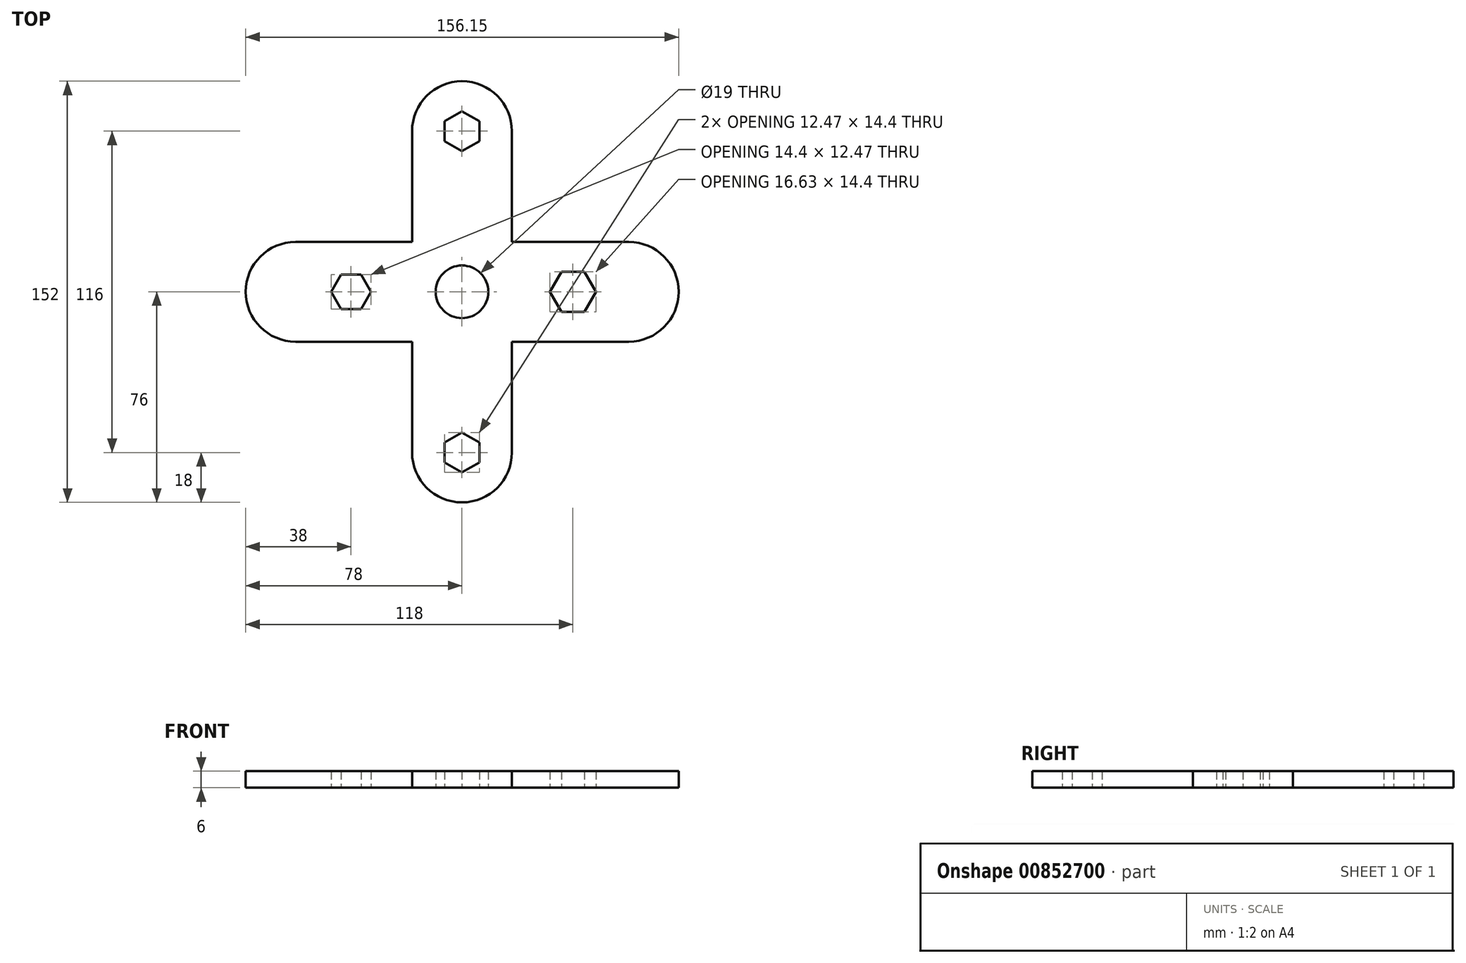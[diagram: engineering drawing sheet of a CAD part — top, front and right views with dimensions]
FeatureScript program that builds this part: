
annotation { "Feature Type Name" : "Feature", "Feature Type Description" : "" }
export const myFeature = defineFeature(function(context is Context, id is Id, definition is map)
    precondition{}
    {
        {
            var Q0;
            Q0=qCreatedBy(makeId("Top.planeOp"),FACE);
            var sketch = newSketch(context, id + "F0", { "sketchPlane" : qUnion([Q0])});
            skCircle(sketch, "E0", {"center": v(0, 0) * mm, "radius": 9.5 * mm});
            skLineSegment(sketch, "E1.bottom", {"start": v(0, 0) * mm, "end": v(-40, 0) * mm});
            skLineSegment(sketch, "E1.top", {"start": v(0, 18) * mm, "end": v(-40, 18) * mm});
            skLineSegment(sketch, "E1.left", {"start": v(0, 0) * mm, "end": v(0, 18) * mm});
            skLineSegment(sketch, "E2.bottom", {"start": v(0, 0) * mm, "end": v(40, 0) * mm});
            skLineSegment(sketch, "E2.top", {"start": v(0, 18) * mm, "end": v(40, 18) * mm});
            skLineSegment(sketch, "E3.top", {"start": v(0, -18) * mm, "end": v(-40, -18) * mm});
            skLineSegment(sketch, "E3.left", {"start": v(0, 0) * mm, "end": v(0, -18) * mm});
            skLineSegment(sketch, "E4.top", {"start": v(0, -18) * mm, "end": v(40, -18) * mm});
            skLineSegment(sketch, "E5.left", {"start": v(0, 0) * mm, "end": v(0, 40) * mm});
            skLineSegment(sketch, "E5.right", {"start": v(-18, 0) * mm, "end": v(-18, 40) * mm});
            skPoint(sketch, "E6.oppositeSnap0", {"position": v(20, 0) * mm});
            skLineSegment(sketch, "E6.bottom", {"start": v(0, 0) * mm, "end": v(20, 0) * mm});
            skLineSegment(sketch, "E6.left", {"start": v(0, 0) * mm, "end": v(0, 58) * mm});
            skLineSegment(sketch, "E7", {"start": v(0, 58) * mm, "end": v(18, 58) * mm});
            skLineSegment(sketch, "E8", {"start": v(18, 58) * mm, "end": v(18, 0) * mm});
            skPoint(sketch, "E9.cCircle.perimeterSnap0", {"position": v(10, 0) * mm});
            skPoint(sketch, "E9.0.midPoint.positionSnap0", {"position": v(10, 0) * mm});
            skLineSegment(sketch, "E10.bottom", {"start": v(-18, 0) * mm, "end": v(0, 0) * mm});
            skLineSegment(sketch, "E10.top", {"start": v(-18, -58) * mm, "end": v(0, -58) * mm});
            skLineSegment(sketch, "E10.left", {"start": v(-18, 0) * mm, "end": v(-18, -58) * mm});
            skLineSegment(sketch, "E10.right", {"start": v(0, 0) * mm, "end": v(0, -58) * mm});
            skLineSegment(sketch, "E11.bottom", {"start": v(0, -18) * mm, "end": v(18, -18) * mm});
            skLineSegment(sketch, "E11.top", {"start": v(0, -58) * mm, "end": v(18, -58) * mm});
            skLineSegment(sketch, "E11.left", {"start": v(0, -18) * mm, "end": v(0, -58) * mm});
            skLineSegment(sketch, "E11.right", {"start": v(18, -18) * mm, "end": v(18, -58) * mm});
            skArc(sketch, "E12", {"start": v(-18, -58) * mm, "mid": v(0, -76) * mm, "end": v(18, -58) * mm});
            skCircle(sketch, "E13.cCircle", {"center": v(0, 58) * mm, "radius": 7.2 * mm, "construction": true});
            skLineSegment(sketch, "E13.0", {"start": v(0, 50.8) * mm, "end": v(-6.24, 54.4) * mm});
            skLineSegment(sketch, "E13.1", {"start": v(-6.24, 54.4) * mm, "end": v(-6.24, 61.6) * mm});
            skLineSegment(sketch, "E13.2", {"start": v(-6.24, 61.6) * mm, "end": v(0, 65.2) * mm});
            skLineSegment(sketch, "E13.3", {"start": v(0, 65.2) * mm, "end": v(6.24, 61.6) * mm});
            skLineSegment(sketch, "E13.4", {"start": v(6.24, 61.6) * mm, "end": v(6.24, 54.4) * mm});
            skLineSegment(sketch, "E13.5", {"start": v(6.24, 54.4) * mm, "end": v(0, 50.8) * mm});
            skCircle(sketch, "E14.cCircle", {"center": v(0, -58) * mm, "radius": 7.2 * mm, "construction": true});
            skLineSegment(sketch, "E14.0", {"start": v(0, -50.8) * mm, "end": v(6.24, -54.4) * mm});
            skLineSegment(sketch, "E14.1", {"start": v(6.24, -54.4) * mm, "end": v(6.24, -61.6) * mm});
            skLineSegment(sketch, "E14.2", {"start": v(6.24, -61.6) * mm, "end": v(0, -65.2) * mm});
            skLineSegment(sketch, "E14.3", {"start": v(0, -65.2) * mm, "end": v(-6.24, -61.6) * mm});
            skLineSegment(sketch, "E14.4", {"start": v(-6.24, -61.6) * mm, "end": v(-6.24, -54.4) * mm});
            skLineSegment(sketch, "E14.5", {"start": v(-6.24, -54.4) * mm, "end": v(0, -50.8) * mm});
            skCircle(sketch, "E15.cCircle", {"center": v(-40, 0) * mm, "radius": 7.2 * mm, "construction": true});
            skLineSegment(sketch, "E15.0", {"start": v(-32.8, 0) * mm, "end": v(-36.4, -6.24) * mm});
            skLineSegment(sketch, "E15.1", {"start": v(-36.4, -6.24) * mm, "end": v(-43.6, -6.24) * mm});
            skLineSegment(sketch, "E15.2", {"start": v(-43.6, -6.24) * mm, "end": v(-47.2, 0) * mm});
            skLineSegment(sketch, "E15.3", {"start": v(-47.2, 0) * mm, "end": v(-43.6, 6.24) * mm});
            skLineSegment(sketch, "E15.4", {"start": v(-43.6, 6.24) * mm, "end": v(-36.4, 6.24) * mm});
            skLineSegment(sketch, "E15.5", {"start": v(-36.4, 6.24) * mm, "end": v(-32.8, 0) * mm});
            skLineSegment(sketch, "E16", {"start": v(0, 58) * mm, "end": v(-18, 58) * mm});
            skLineSegment(sketch, "E17", {"start": v(-18, 40) * mm, "end": v(-18, 58) * mm});
            skArc(sketch, "E18", {"start": v(18, 58) * mm, "mid": v(0, 76) * mm, "end": v(-18, 58) * mm});
            skLineSegment(sketch, "E19", {"start": v(-40, 0) * mm, "end": v(-60, 0) * mm});
            skLineSegment(sketch, "E20", {"start": v(-60, -18) * mm, "end": v(-40, -18) * mm});
            skLineSegment(sketch, "E21", {"start": v(-60, 18) * mm, "end": v(-40, 18) * mm});
            skArc(sketch, "E22", {"start": v(-60, 18) * mm, "mid": v(-78, 0) * mm, "end": v(-60, -18) * mm});
            skLineSegment(sketch, "E23.bottom", {"start": v(20, 0) * mm, "end": v(30.96, 0) * mm});
            skLineSegment(sketch, "E24.bottom", {"start": v(40, 0) * mm, "end": v(60.15, 0) * mm});
            skLineSegment(sketch, "E24.top", {"start": v(40, 18) * mm, "end": v(60.15, 18) * mm});
            skLineSegment(sketch, "E25.top", {"start": v(40, -18) * mm, "end": v(60.15, -18) * mm});
            skLineSegment(sketch, "E26.bottom", {"start": v(40, -12.83) * mm, "end": v(40, -12.83) * mm});
            skLineSegment(sketch, "E26.top", {"start": v(40, 9) * mm, "end": v(40, 9) * mm});
            skCircle(sketch, "E27.cCircle", {"center": v(40, 0) * mm, "radius": 7.2 * mm, "construction": true});
            skLineSegment(sketch, "E27.0", {"start": v(35.84, 7.2) * mm, "end": v(44.16, 7.2) * mm});
            skLineSegment(sketch, "E27.1", {"start": v(44.16, 7.2) * mm, "end": v(48.31, 0) * mm});
            skLineSegment(sketch, "E27.2", {"start": v(48.31, 0) * mm, "end": v(44.16, -7.2) * mm});
            skLineSegment(sketch, "E27.3", {"start": v(44.16, -7.2) * mm, "end": v(35.84, -7.2) * mm});
            skLineSegment(sketch, "E27.4", {"start": v(35.84, -7.2) * mm, "end": v(31.69, 0) * mm});
            skLineSegment(sketch, "E27.5", {"start": v(31.69, 0) * mm, "end": v(35.84, 7.2) * mm});
            skPoint(sketch, "E27.0.midPoint", {"position": v(40, 7.2) * mm});
            skArc(sketch, "E28", {"start": v(60.15, -18) * mm, "mid": v(78.15, 0) * mm, "end": v(60.15, 18) * mm});
            skSolve(sketch);
        }
        {
            var Q0;
            Q0=makeQuery(id+"F0.imprint","IMPRINT",FACE,{"disambiguationData":[TD([[makeQuery(id+"F0.imprint","IMPRINT",EDGE,{"derivedFrom":sQuery(id+"F0.wireOp",EDGE,"E15.0")}),1.0]])]});
            var Q1;
            {var subQ3=sQuery(id+"F0.wireOp",EDGE,"E0");var subQ6=sQuery(id+"F0.wireOp",EDGE,"E1.bottom");var subQ8=makeQuery(id+"F0.imprint","INTERSECT",VERTEX,{"derivedFrom":[subQ3,subQ6]});Q1=makeQuery(id+"F0.imprint","IMPRINT",FACE,{"disambiguationData":[TD([[makeQuery(id+"F0.imprint","IMPRINT",EDGE,{"disambiguationData":[TD([[subQ8,-1.0]])],"derivedFrom":subQ3}),-1.0]])]});}
            var Q2;
            {var subQ3=sQuery(id+"F0.wireOp",EDGE,"E1.left");var subQ5=sQuery(id+"F0.wireOp",EDGE,"E0");var subQ6=makeQuery(id+"F0.imprint","INTERSECT",VERTEX,{"derivedFrom":[subQ5,subQ3]});Q2=makeQuery(id+"F0.imprint","IMPRINT",FACE,{"disambiguationData":[TD([[makeQuery(id+"F0.imprint","IMPRINT",EDGE,{"disambiguationData":[TD([[subQ6,-1.0]])],"derivedFrom":subQ5}),-1.0]])]});}
            var Q3;
            {var subQ3=sQuery(id+"F0.wireOp",EDGE,"E0");var subQ6=sQuery(id+"F0.wireOp",EDGE,"E1.left");var subQ9=makeQuery(id+"F0.imprint","INTERSECT",VERTEX,{"derivedFrom":[subQ3,subQ6]});Q3=makeQuery(id+"F0.imprint","IMPRINT",FACE,{"disambiguationData":[TD([[makeQuery(id+"F0.imprint","IMPRINT",EDGE,{"disambiguationData":[TD([[subQ9,1.0]])],"derivedFrom":subQ3}),-1.0]])]});}
            var Q4;
            {var subQ1=sQuery(id+"F0.wireOp",EDGE,"E24.top");Q4=makeQuery(id+"F0.imprint","IMPRINT",FACE,{"disambiguationData":[TD([[makeQuery(id+"F0.imprint","IMPRINT",EDGE,{"derivedFrom":subQ1}),-1.0]])]});}
            var Q5;
            {var subQ3=sQuery(id+"F0.wireOp",EDGE,"E14.5");Q5=makeQuery(id+"F0.imprint","IMPRINT",FACE,{"disambiguationData":[TD([[makeQuery(id+"F0.imprint","IMPRINT",EDGE,{"derivedFrom":subQ3}),1.0]])]});}
            var Q6;
            {var subQ0=sQuery(id+"F0.wireOp",EDGE,"E11.right");Q6=makeQuery(id+"F0.imprint","IMPRINT",FACE,{"disambiguationData":[TD([[makeQuery(id+"F0.imprint","IMPRINT",EDGE,{"derivedFrom":subQ0}),-1.0]])]});}
            var Q7;
            {var subQ0=sQuery(id+"F0.wireOp",EDGE,"E12");Q7=makeQuery(id+"F0.imprint","IMPRINT",FACE,{"disambiguationData":[TD([[makeQuery(id+"F0.imprint","IMPRINT",EDGE,{"derivedFrom":subQ0}),1.0]])]});}
            var Q8;
            {var subQ5=sQuery(id+"F0.wireOp",EDGE,"E5.left");Q8=makeQuery(id+"F0.imprint","IMPRINT",FACE,{"disambiguationData":[TD([[makeQuery(id+"F0.imprint","IMPRINT",EDGE,{"derivedFrom":subQ5}),-1.0]])]});}
            var Q9;
            {var subQ1=sQuery(id+"F0.wireOp",EDGE,"E5.left");Q9=makeQuery(id+"F0.imprint","IMPRINT",FACE,{"disambiguationData":[TD([[makeQuery(id+"F0.imprint","IMPRINT",EDGE,{"derivedFrom":subQ1}),1.0]])]});}
            var Q10;
            {var subQ1=sQuery(id+"F0.wireOp",EDGE,"E13.2");Q10=makeQuery(id+"F0.imprint","IMPRINT",FACE,{"disambiguationData":[TD([[makeQuery(id+"F0.imprint","IMPRINT",EDGE,{"derivedFrom":subQ1}),1.0]])]});}
            extrude(context, id + "F1", {"entities" : qUnion([Q0, Q1, Q2, Q3, Q4, Q5, Q6, Q7, Q8, Q9, Q10]), "depth" : 6 * mm, "offsetDistance" : 25 * mm});
        }
    });
